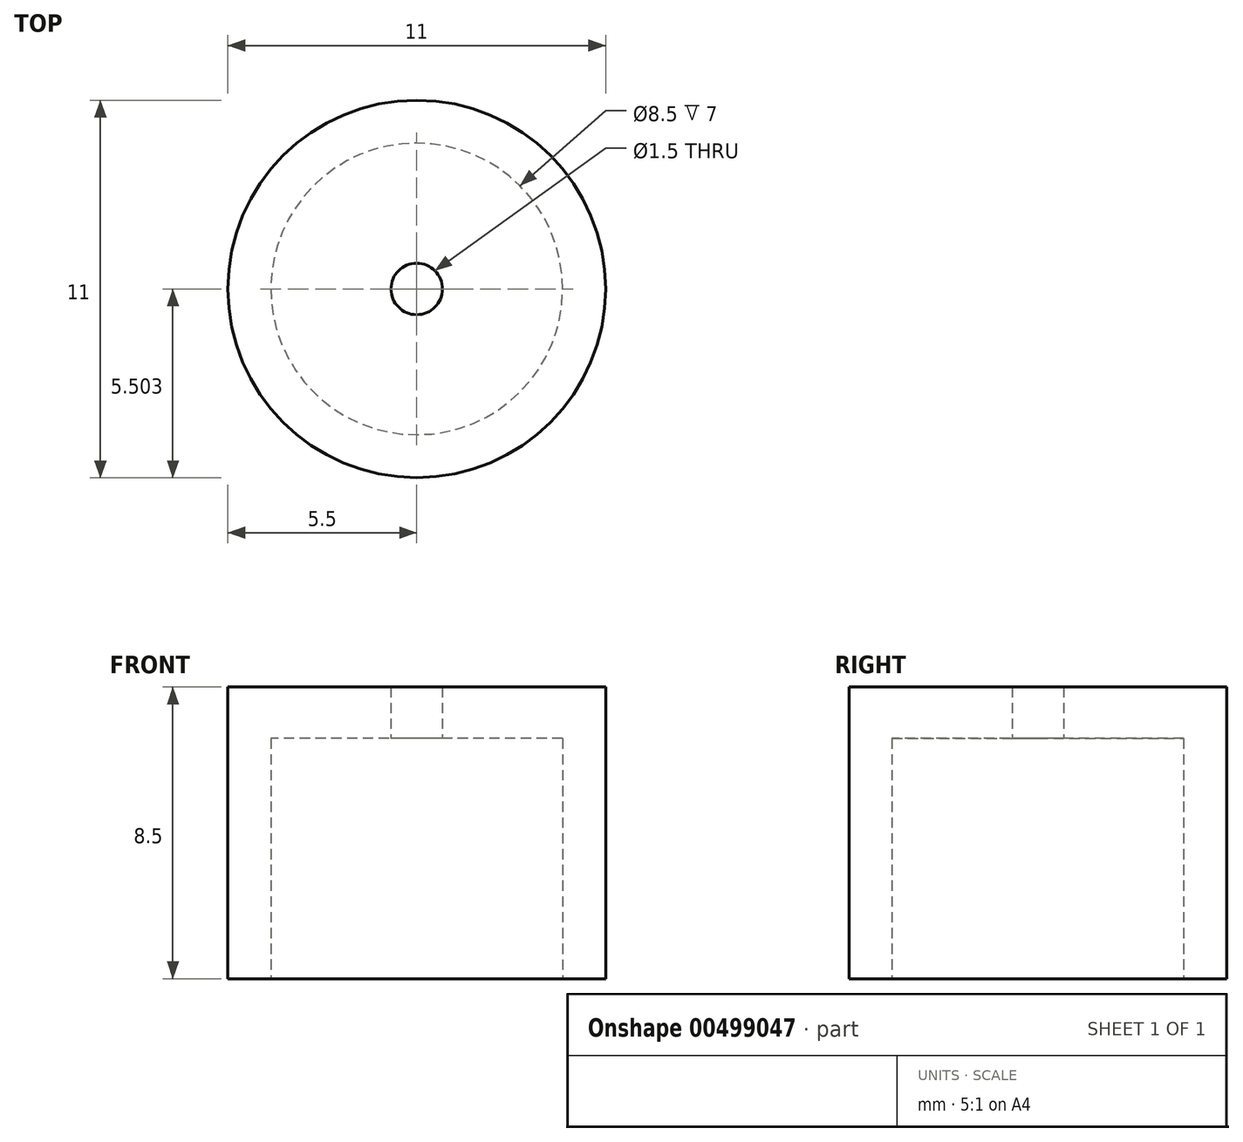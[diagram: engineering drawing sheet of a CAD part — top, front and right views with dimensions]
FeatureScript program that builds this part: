
annotation { "Feature Type Name" : "Feature", "Feature Type Description" : "" }
export const myFeature = defineFeature(function(context is Context, id is Id, definition is map)
    precondition{}
    {
        {
            var Q0;
            Q0=qCreatedBy(makeId("Top.planeOp"),FACE);
            var sketch = newSketch(context, id + "F0", { "sketchPlane" : qUnion([Q0])});
            skCircle(sketch, "E0", {"center": v(0, -0.55) * mm, "radius": 5.5 * mm});
            skCircle(sketch, "E1", {"center": v(0, -0.55) * mm, "radius": 4.25 * mm});
            skSolve(sketch);
        }
        {
            var Q0;
            Q0=makeQuery(id+"F0.imprint","IMPRINT",FACE,{"disambiguationData":[TD([[makeQuery(id+"F0.imprint","IMPRINT",EDGE,{"derivedFrom":sQuery(id+"F0.wireOp",EDGE,"E0")}),1.0]])]});
            var Q1;
            Q1=makeQuery(id+"F0.imprint","IMPRINT",FACE,{"disambiguationData":[TD([[makeQuery(id+"F0.imprint","IMPRINT",EDGE,{"derivedFrom":sQuery(id+"F0.wireOp",EDGE,"E1")}),1.0]])]});
            extrude(context, id + "F1", {"entities" : qUnion([Q0, Q1]), "depth" : 8.5 * mm, "offsetDistance" : 25 * mm});
        }
        {
            var Q0;
            Q0=makeQuery(id+"F0.imprint","IMPRINT",FACE,{"disambiguationData":[TD([[makeQuery(id+"F0.imprint","IMPRINT",EDGE,{"derivedFrom":sQuery(id+"F0.wireOp",EDGE,"E1")}),1.0]])]});
            extrude(context, id + "F2", {"entities" : qUnion([Q0]), "operationType" : NewBodyOperationType.REMOVE, "depth" : 7 * mm, "offsetDistance" : 25 * mm});
        }
        {
            var Q0;
            Q0=sQuery(id+"F0.wireOp",VERTEX,"E0.center");
            var Q1;
            Q1=makeQuery(id+"F1.opExtrude","SWEPT_BODY",BODY,{"disambiguationData":[OSD([sQuery(id+"F0.wireOp",EDGE,"E0")])]});
            hole(context, id + "F3", {"style" : HoleStyle.SIMPLE, "endStyle" : HoleEndStyle.THROUGH, "oppositeDirection" : true, "holeDiameter" : 1.5 * mm, "isTappedThrough" : true, "tappedDepth" : 12 * mm, "tapClearance" : 3, "locations" : qUnion([Q0]), "scope" : qUnion([Q1])});
        }
    });
